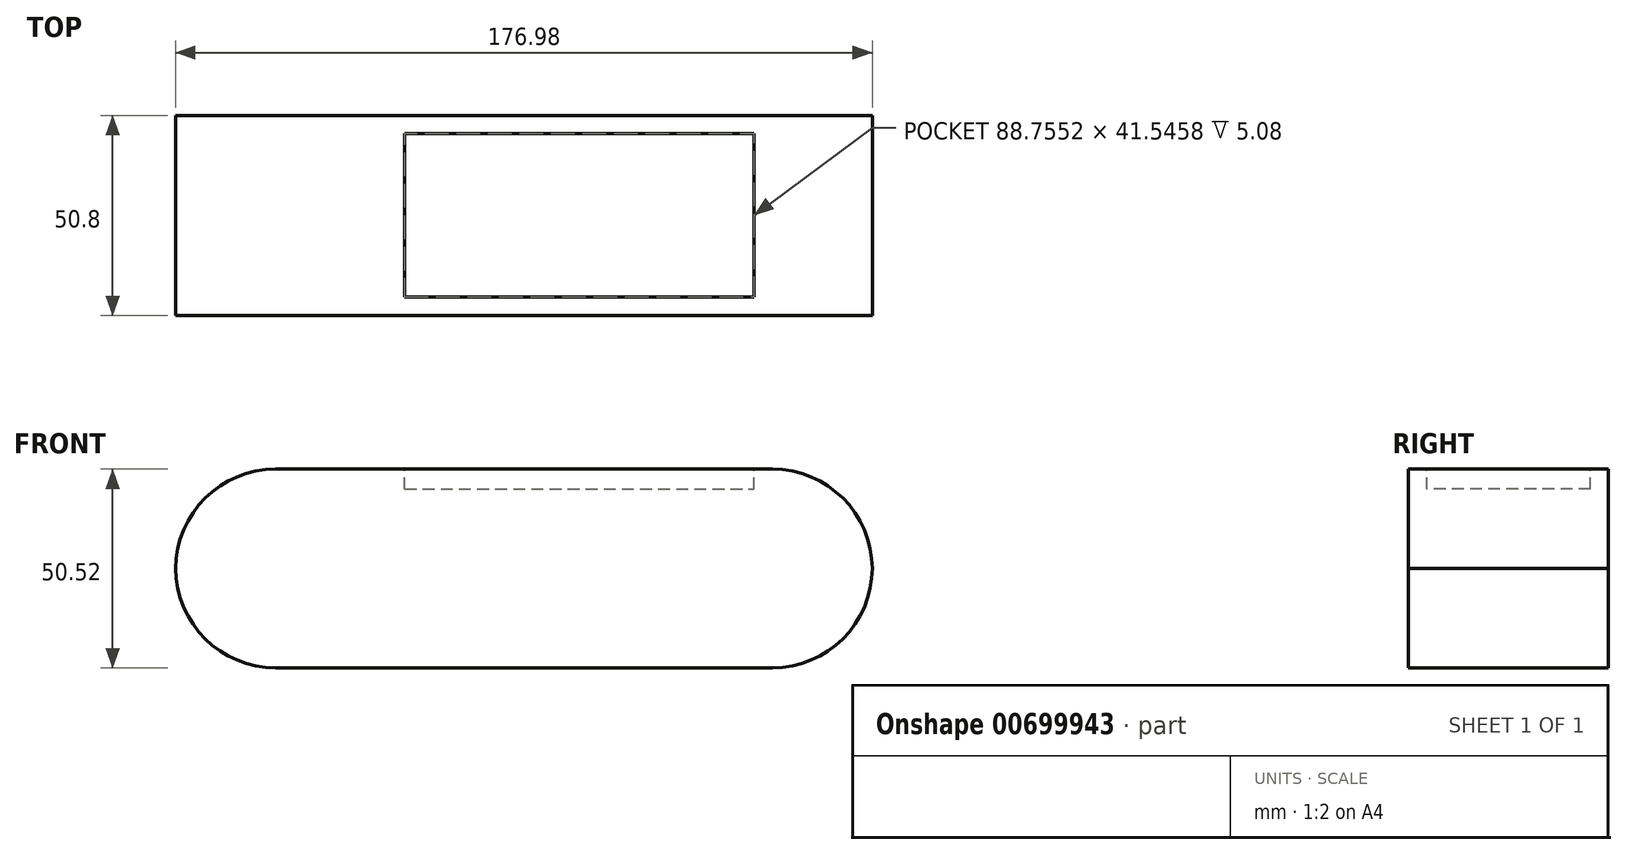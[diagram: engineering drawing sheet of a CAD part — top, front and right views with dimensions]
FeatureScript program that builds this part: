
annotation { "Feature Type Name" : "Feature", "Feature Type Description" : "" }
export const myFeature = defineFeature(function(context is Context, id is Id, definition is map)
    precondition{}
    {
        {
            var Q0;
            Q0=qCreatedBy(makeId("Front.planeOp"),FACE);
            var sketch = newSketch(context, id + "F0", { "sketchPlane" : qUnion([Q0])});
            skLineSegment(sketch, "E0.bottom", {"start": v(-58.18, 16.85) * mm, "end": v(118.8, 16.85) * mm});
            skLineSegment(sketch, "E0.top", {"start": v(-58.18, -33.67) * mm, "end": v(118.8, -33.67) * mm});
            skLineSegment(sketch, "E0.left", {"start": v(-58.18, 16.85) * mm, "end": v(-58.18, -33.67) * mm});
            skLineSegment(sketch, "E0.right", {"start": v(118.8, 16.85) * mm, "end": v(118.8, -33.67) * mm});
            skSolve(sketch);
        }
        {
            var Q0;
            Q0=makeQuery(id+"F0.imprint","IMPRINT",FACE,{"disambiguationData":[TD([[makeQuery(id+"F0.imprint","IMPRINT",EDGE,{"derivedFrom":sQuery(id+"F0.wireOp",EDGE,"E0.bottom")}),-1.0]])]});
            extrude(context, id + "F1", {"entities" : qUnion([Q0]), "depth" : 50.8 * mm, "offsetDistance" : 25.4 * mm});
        }
        {
            var Q0;
            Q0=makeQuery(id+"F1.opExtrude","SWEPT_EDGE",EDGE,{"disambiguationData":[OSD([sQuery(id+"F0.wireOp",EDGE,"E0.bottom"),sQuery(id+"F0.wireOp",EDGE,"E0.left")])]});
            var Q1;
            Q1=makeQuery(id+"F1.opExtrude","SWEPT_EDGE",EDGE,{"disambiguationData":[OSD([sQuery(id+"F0.wireOp",EDGE,"E0.top"),sQuery(id+"F0.wireOp",EDGE,"E0.left")])]});
            var Q2;
            Q2=makeQuery(id+"F1.opExtrude","SWEPT_EDGE",EDGE,{"disambiguationData":[OSD([sQuery(id+"F0.wireOp",EDGE,"E0.bottom"),sQuery(id+"F0.wireOp",EDGE,"E0.right")])]});
            var Q3;
            Q3=makeQuery(id+"F1.opExtrude","SWEPT_EDGE",EDGE,{"disambiguationData":[OSD([sQuery(id+"F0.wireOp",EDGE,"E0.top"),sQuery(id+"F0.wireOp",EDGE,"E0.right")])]});
            fillet(context, id + "F2", {"entities" : qUnion([Q0, Q1, Q2, Q3]), "radius" : 25.4 * mm, "tangentPropagation" : true, "allowEdgeOverflow" : false});
        }
        {
            var Q0;
            Q0=makeQuery(id+"F1.opExtrude","SWEPT_FACE",FACE,{"disambiguationData":[OSD([sQuery(id+"F0.wireOp",EDGE,"E0.bottom")])]});
            var sketch = newSketch(context, id + "F3", { "sketchPlane" : qUnion([Q0])});
            skLineSegment(sketch, "E1.bottom", {"start": v(0, -4.57) * mm, "end": v(88.76, -4.57) * mm});
            skLineSegment(sketch, "E1.top", {"start": v(0, -46.11) * mm, "end": v(88.76, -46.11) * mm});
            skLineSegment(sketch, "E1.left", {"start": v(0, -4.57) * mm, "end": v(0, -46.11) * mm});
            skLineSegment(sketch, "E1.right", {"start": v(88.76, -4.57) * mm, "end": v(88.76, -46.11) * mm});
            skSolve(sketch);
        }
        {
            var Q0;
            Q0=makeQuery(id+"F3.imprint","IMPRINT",FACE,{"disambiguationData":[TD([[makeQuery(id+"F3.imprint","IMPRINT",EDGE,{"derivedFrom":sQuery(id+"F3.wireOp",EDGE,"E1.bottom")}),-1.0]])]});
            extrude(context, id + "F4", {"entities" : qUnion([Q0]), "operationType" : NewBodyOperationType.REMOVE, "oppositeDirection" : true, "depth" : 5.08 * mm, "offsetDistance" : 25.4 * mm});
        }
    });
